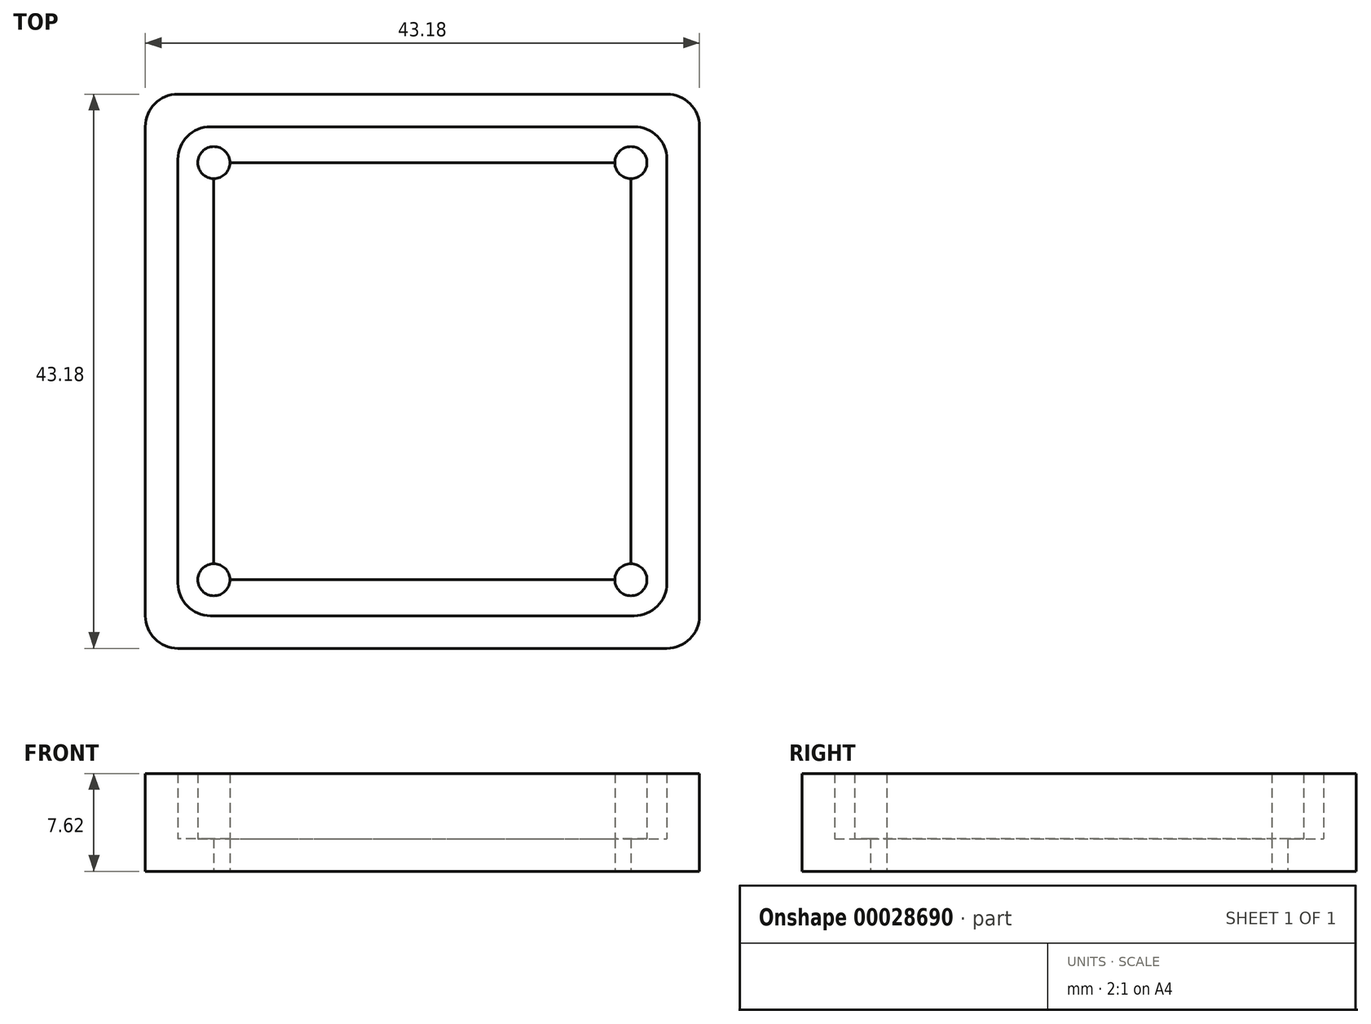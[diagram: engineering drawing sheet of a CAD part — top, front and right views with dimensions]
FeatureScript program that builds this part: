
annotation { "Feature Type Name" : "Feature", "Feature Type Description" : "" }
export const myFeature = defineFeature(function(context is Context, id is Id, definition is map)
    precondition{}
    {
        {
            var Q0;
            Q0=qCreatedBy(makeId("Top.planeOp"),FACE);
            var sketch = newSketch(context, id + "F0", { "sketchPlane" : qUnion([Q0])});
            skLineSegment(sketch, "E0", {"start": v(0, -16.25) * mm, "end": v(0, -19.05) * mm});
            skLineSegment(sketch, "E1.right", {"start": v(19.05, 19.05) * mm, "end": v(19.05, -19.05) * mm});
            skLineSegment(sketch, "E2", {"start": v(-16.25, 0) * mm, "end": v(-19.05, 0) * mm});
            skLineSegment(sketch, "E3", {"start": v(16.25, 0) * mm, "end": v(19.05, 0) * mm});
            skLineSegment(sketch, "E4.bottom", {"start": v(-16.25, -16.25) * mm, "end": v(16.25, -16.25) * mm});
            skLineSegment(sketch, "E4.top", {"start": v(-16.25, 16.25) * mm, "end": v(16.25, 16.25) * mm});
            skLineSegment(sketch, "E4.left", {"start": v(-16.25, -16.25) * mm, "end": v(-16.25, 16.25) * mm});
            skLineSegment(sketch, "E4.right", {"start": v(16.25, -16.25) * mm, "end": v(16.25, 16.25) * mm});
            skCircle(sketch, "E5", {"center": v(-16.25, 16.25) * mm, "radius": 1.25 * mm});
            skCircle(sketch, "E6", {"center": v(16.25, 16.25) * mm, "radius": 1.25 * mm});
            skCircle(sketch, "E7", {"center": v(16.25, -16.25) * mm, "radius": 1.25 * mm});
            skCircle(sketch, "E8", {"center": v(-16.25, -16.25) * mm, "radius": 1.25 * mm});
            skLineSegment(sketch, "E9", {"start": v(0, 16.25) * mm, "end": v(0, -16.25) * mm});
            skLineSegment(sketch, "E10", {"start": v(-16.25, 0) * mm, "end": v(16.25, 0) * mm});
            skLineSegment(sketch, "E1.bottom", {"start": v(-19.05, 19.05) * mm, "end": v(19.05, 19.05) * mm});
            skLineSegment(sketch, "E1.top", {"start": v(-19.05, -19.05) * mm, "end": v(19.05, -19.05) * mm});
            skLineSegment(sketch, "E1.left", {"start": v(-19.05, 19.05) * mm, "end": v(-19.05, -19.05) * mm});
            skLineSegment(sketch, "E11", {"start": v(0, 16.25) * mm, "end": v(0, 19.05) * mm});
            skLineSegment(sketch, "E12.bottom", {"start": v(-21.59, 21.6) * mm, "end": v(21.59, 21.6) * mm});
            skLineSegment(sketch, "E12.top", {"start": v(-21.59, -21.59) * mm, "end": v(21.59, -21.59) * mm});
            skLineSegment(sketch, "E12.left", {"start": v(-21.59, 21.6) * mm, "end": v(-21.59, -21.59) * mm});
            skLineSegment(sketch, "E12.right", {"start": v(21.6, 21.6) * mm, "end": v(21.6, -21.59) * mm});
            skLineSegment(sketch, "E13.bottom", {"start": v(-10.16, 10.16) * mm, "end": v(10.16, 10.16) * mm});
            skLineSegment(sketch, "E13.top", {"start": v(-10.16, -10.16) * mm, "end": v(10.16, -10.16) * mm});
            skLineSegment(sketch, "E13.left", {"start": v(-10.16, 10.16) * mm, "end": v(-10.16, -10.16) * mm});
            skLineSegment(sketch, "E13.right", {"start": v(10.16, 10.16) * mm, "end": v(10.16, -10.16) * mm});
            skLineSegment(sketch, "E14", {"start": v(10.16, 0) * mm, "end": v(16.25, 0) * mm});
            skLineSegment(sketch, "E15", {"start": v(0, -10.16) * mm, "end": v(0, -16.25) * mm});
            skLineSegment(sketch, "E16", {"start": v(0, 10.16) * mm, "end": v(0, 16.25) * mm});
            skLineSegment(sketch, "E17", {"start": v(-10.16, 0) * mm, "end": v(-16.25, 0) * mm});
            skSolve(sketch);
        }
        {
            var Q0;
            {var subQ6=sQuery(id+"F0.wireOp",EDGE,"E3");Q0=makeQuery(id+"F0.imprint","IMPRINT",FACE,{"disambiguationData":[TD([[makeQuery(id+"F0.imprint","IMPRINT",EDGE,{"derivedFrom":subQ6}),1.0]])]});}
            var Q1;
            {var subQ4=sQuery(id+"F0.wireOp",EDGE,"E2");Q1=makeQuery(id+"F0.imprint","IMPRINT",FACE,{"disambiguationData":[TD([[makeQuery(id+"F0.imprint","IMPRINT",EDGE,{"derivedFrom":subQ4}),-1.0]])]});}
            var Q2;
            {var subQ4=sQuery(id+"F0.wireOp",EDGE,"E0");Q2=makeQuery(id+"F0.imprint","IMPRINT",FACE,{"disambiguationData":[TD([[makeQuery(id+"F0.imprint","IMPRINT",EDGE,{"derivedFrom":subQ4}),-1.0]])]});}
            var Q3;
            {var subQ3=sQuery(id+"F0.wireOp",EDGE,"E0");Q3=makeQuery(id+"F0.imprint","IMPRINT",FACE,{"disambiguationData":[TD([[makeQuery(id+"F0.imprint","IMPRINT",EDGE,{"derivedFrom":subQ3}),1.0]])]});}
            var Q4;
            {var subQ1=sQuery(id+"F0.wireOp",EDGE,"E15");Q4=makeQuery(id+"F0.imprint","IMPRINT",FACE,{"disambiguationData":[TD([[makeQuery(id+"F0.imprint","IMPRINT",EDGE,{"derivedFrom":subQ1}),1.0]])]});}
            var Q5;
            {var subQ1=sQuery(id+"F0.wireOp",EDGE,"E15");Q5=makeQuery(id+"F0.imprint","IMPRINT",FACE,{"disambiguationData":[TD([[makeQuery(id+"F0.imprint","IMPRINT",EDGE,{"derivedFrom":subQ1}),-1.0]])]});}
            var Q6;
            {var subQ1=sQuery(id+"F0.wireOp",EDGE,"E16");Q6=makeQuery(id+"F0.imprint","IMPRINT",FACE,{"disambiguationData":[TD([[makeQuery(id+"F0.imprint","IMPRINT",EDGE,{"derivedFrom":subQ1}),1.0]])]});}
            var Q7;
            {var subQ4=sQuery(id+"F0.wireOp",EDGE,"E16");Q7=makeQuery(id+"F0.imprint","IMPRINT",FACE,{"disambiguationData":[TD([[makeQuery(id+"F0.imprint","IMPRINT",EDGE,{"derivedFrom":subQ4}),-1.0]])]});}
            extrude(context, id + "F1", {"entities" : qUnion([Q0, Q1, Q2, Q3, Q4, Q5, Q6, Q7]), "depth" : 2.54 * mm});
        }
        {
            var Q0;
            Q0 = qSketchRegion(id + "F0", true);
            var Q1;
            Q1=makeQuery(id+"F1.opExtrude","CAP_FACE",FACE,{"disambiguationData":[OSD([sQuery(id+"F0.wireOp",EDGE,"E12.bottom"),sQuery(id+"F0.wireOp",EDGE,"E12.top"),sQuery(id+"F0.wireOp",EDGE,"E12.left"),sQuery(id+"F0.wireOp",EDGE,"E12.right")])],"isStart":false});
            extrude(context, id + "F2", {"entities" : qUnion([Q0, Q1]), "operationType" : NewBodyOperationType.ADD, "depth" : 7.62 * mm});
        }
        {
            var Q0;
            Q0=makeQuery(id+"F2.opExtrude","SWEPT_EDGE",EDGE,{"disambiguationData":[OSD([sQuery(id+"F0.wireOp",EDGE,"E1.right"),sQuery(id+"F0.wireOp",EDGE,"E1.bottom")])]});
            var Q1;
            Q1=makeQuery(id+"F2.opExtrude","SWEPT_EDGE",EDGE,{"disambiguationData":[OSD([sQuery(id+"F0.wireOp",EDGE,"E1.bottom"),sQuery(id+"F0.wireOp",EDGE,"E1.left")])]});
            var Q2;
            Q2=makeQuery(id+"F2.opExtrude","SWEPT_EDGE",EDGE,{"disambiguationData":[OSD([sQuery(id+"F0.wireOp",EDGE,"E1.top"),sQuery(id+"F0.wireOp",EDGE,"E1.left")])]});
            var Q3;
            Q3=makeQuery(id+"F2.opExtrude","SWEPT_EDGE",EDGE,{"disambiguationData":[OSD([sQuery(id+"F0.wireOp",EDGE,"E1.right"),sQuery(id+"F0.wireOp",EDGE,"E1.top")])]});
            var Q4;
            Q4=makeQuery(id+"F2.opExtrude","SWEPT_EDGE",EDGE,{"disambiguationData":[OSD([sQuery(id+"F0.wireOp",EDGE,"E12.bottom"),sQuery(id+"F0.wireOp",EDGE,"E12.left")])]});
            var Q5;
            Q5=makeQuery(id+"F2.opExtrude","SWEPT_EDGE",EDGE,{"disambiguationData":[OSD([sQuery(id+"F0.wireOp",EDGE,"E12.bottom"),sQuery(id+"F0.wireOp",EDGE,"E12.right")])]});
            var Q6;
            Q6=makeQuery(id+"F2.opExtrude","SWEPT_EDGE",EDGE,{"disambiguationData":[OSD([sQuery(id+"F0.wireOp",EDGE,"E12.top"),sQuery(id+"F0.wireOp",EDGE,"E12.left")])]});
            var Q7;
            Q7=makeQuery(id+"F2.opExtrude","SWEPT_EDGE",EDGE,{"disambiguationData":[OSD([sQuery(id+"F0.wireOp",EDGE,"E12.top"),sQuery(id+"F0.wireOp",EDGE,"E12.right")])]});
            var Q8;
            Q8=makeQuery(id+"F1.opExtrude","SWEPT_EDGE",EDGE,{"disambiguationData":[OSD([sQuery(id+"F0.wireOp",EDGE,"E13.bottom"),sQuery(id+"F0.wireOp",EDGE,"E13.right")])]});
            var Q9;
            Q9=makeQuery(id+"F1.opExtrude","SWEPT_EDGE",EDGE,{"disambiguationData":[OSD([sQuery(id+"F0.wireOp",EDGE,"E13.top"),sQuery(id+"F0.wireOp",EDGE,"E13.left")])]});
            var Q10;
            Q10=makeQuery(id+"F1.opExtrude","SWEPT_EDGE",EDGE,{"disambiguationData":[OSD([sQuery(id+"F0.wireOp",EDGE,"E13.top"),sQuery(id+"F0.wireOp",EDGE,"E13.right")])]});
            var Q11;
            Q11=makeQuery(id+"F1.opExtrude","SWEPT_EDGE",EDGE,{"disambiguationData":[OSD([sQuery(id+"F0.wireOp",EDGE,"E13.bottom"),sQuery(id+"F0.wireOp",EDGE,"E13.left")])]});
            fillet(context, id + "F3", {"entities" : qUnion([Q0, Q1, Q2, Q3, Q4, Q5, Q6, Q7, Q8, Q9, Q10, Q11]), "radius" : 2.54 * mm, "tangentPropagation" : true, "allowEdgeOverflow" : false});
        }
        {
            var Q0;
            {var subQ1=sQuery(id+"F0.wireOp",EDGE,"E4.left");var subQ3=sQuery(id+"F0.wireOp",EDGE,"E4.top");var subQ5=makeQuery(id+"F0.imprint","INTERSECT",VERTEX,{"derivedFrom":[subQ3,subQ1]});Q0=makeQuery(id+"F0.imprint","IMPRINT",FACE,{"disambiguationData":[TD([[makeQuery(id+"F0.imprint","IMPRINT",EDGE,{"disambiguationData":[TD([[subQ5,-1.0]])],"derivedFrom":subQ3}),1.0]])]});}
            var Q1;
            {var subQ1=sQuery(id+"F0.wireOp",EDGE,"E4.left");var subQ3=sQuery(id+"F0.wireOp",EDGE,"E4.top");var subQ5=makeQuery(id+"F0.imprint","INTERSECT",VERTEX,{"derivedFrom":[subQ3,subQ1]});Q1=makeQuery(id+"F0.imprint","IMPRINT",FACE,{"disambiguationData":[TD([[makeQuery(id+"F0.imprint","IMPRINT",EDGE,{"disambiguationData":[TD([[subQ5,-1.0]])],"derivedFrom":subQ3}),-1.0]])]});}
            var Q2;
            {var subQ1=sQuery(id+"F0.wireOp",EDGE,"E4.right");var subQ3=sQuery(id+"F0.wireOp",EDGE,"E4.top");var subQ5=makeQuery(id+"F0.imprint","INTERSECT",VERTEX,{"derivedFrom":[subQ3,subQ1]});Q2=makeQuery(id+"F0.imprint","IMPRINT",FACE,{"disambiguationData":[TD([[makeQuery(id+"F0.imprint","IMPRINT",EDGE,{"disambiguationData":[TD([[subQ5,1.0]])],"derivedFrom":subQ3}),1.0]])]});}
            var Q3;
            {var subQ1=sQuery(id+"F0.wireOp",EDGE,"E4.right");var subQ3=sQuery(id+"F0.wireOp",EDGE,"E4.top");var subQ5=makeQuery(id+"F0.imprint","INTERSECT",VERTEX,{"derivedFrom":[subQ3,subQ1]});Q3=makeQuery(id+"F0.imprint","IMPRINT",FACE,{"disambiguationData":[TD([[makeQuery(id+"F0.imprint","IMPRINT",EDGE,{"disambiguationData":[TD([[subQ5,1.0]])],"derivedFrom":subQ3}),-1.0]])]});}
            var Q4;
            {var subQ1=sQuery(id+"F0.wireOp",EDGE,"E4.right");var subQ3=sQuery(id+"F0.wireOp",EDGE,"E4.bottom");var subQ5=makeQuery(id+"F0.imprint","INTERSECT",VERTEX,{"derivedFrom":[subQ3,subQ1]});Q4=makeQuery(id+"F0.imprint","IMPRINT",FACE,{"disambiguationData":[TD([[makeQuery(id+"F0.imprint","IMPRINT",EDGE,{"disambiguationData":[TD([[subQ5,1.0]])],"derivedFrom":subQ3}),-1.0]])]});}
            var Q5;
            {var subQ1=sQuery(id+"F0.wireOp",EDGE,"E4.right");var subQ3=sQuery(id+"F0.wireOp",EDGE,"E4.bottom");var subQ5=makeQuery(id+"F0.imprint","INTERSECT",VERTEX,{"derivedFrom":[subQ3,subQ1]});Q5=makeQuery(id+"F0.imprint","IMPRINT",FACE,{"disambiguationData":[TD([[makeQuery(id+"F0.imprint","IMPRINT",EDGE,{"disambiguationData":[TD([[subQ5,1.0]])],"derivedFrom":subQ3}),1.0]])]});}
            var Q6;
            {var subQ1=sQuery(id+"F0.wireOp",EDGE,"E4.left");var subQ3=sQuery(id+"F0.wireOp",EDGE,"E4.bottom");var subQ5=makeQuery(id+"F0.imprint","INTERSECT",VERTEX,{"derivedFrom":[subQ3,subQ1]});Q6=makeQuery(id+"F0.imprint","IMPRINT",FACE,{"disambiguationData":[TD([[makeQuery(id+"F0.imprint","IMPRINT",EDGE,{"disambiguationData":[TD([[subQ5,-1.0]])],"derivedFrom":subQ3}),-1.0]])]});}
            var Q7;
            {var subQ1=sQuery(id+"F0.wireOp",EDGE,"E4.left");var subQ3=sQuery(id+"F0.wireOp",EDGE,"E4.bottom");var subQ5=makeQuery(id+"F0.imprint","INTERSECT",VERTEX,{"derivedFrom":[subQ3,subQ1]});Q7=makeQuery(id+"F0.imprint","IMPRINT",FACE,{"disambiguationData":[TD([[makeQuery(id+"F0.imprint","IMPRINT",EDGE,{"disambiguationData":[TD([[subQ5,-1.0]])],"derivedFrom":subQ3}),1.0]])]});}
            extrude(context, id + "F4", {"entities" : qUnion([Q0, Q1, Q2, Q3, Q4, Q5, Q6, Q7]), "operationType" : NewBodyOperationType.ADD, "depth" : 7.62 * mm});
        }
    });
